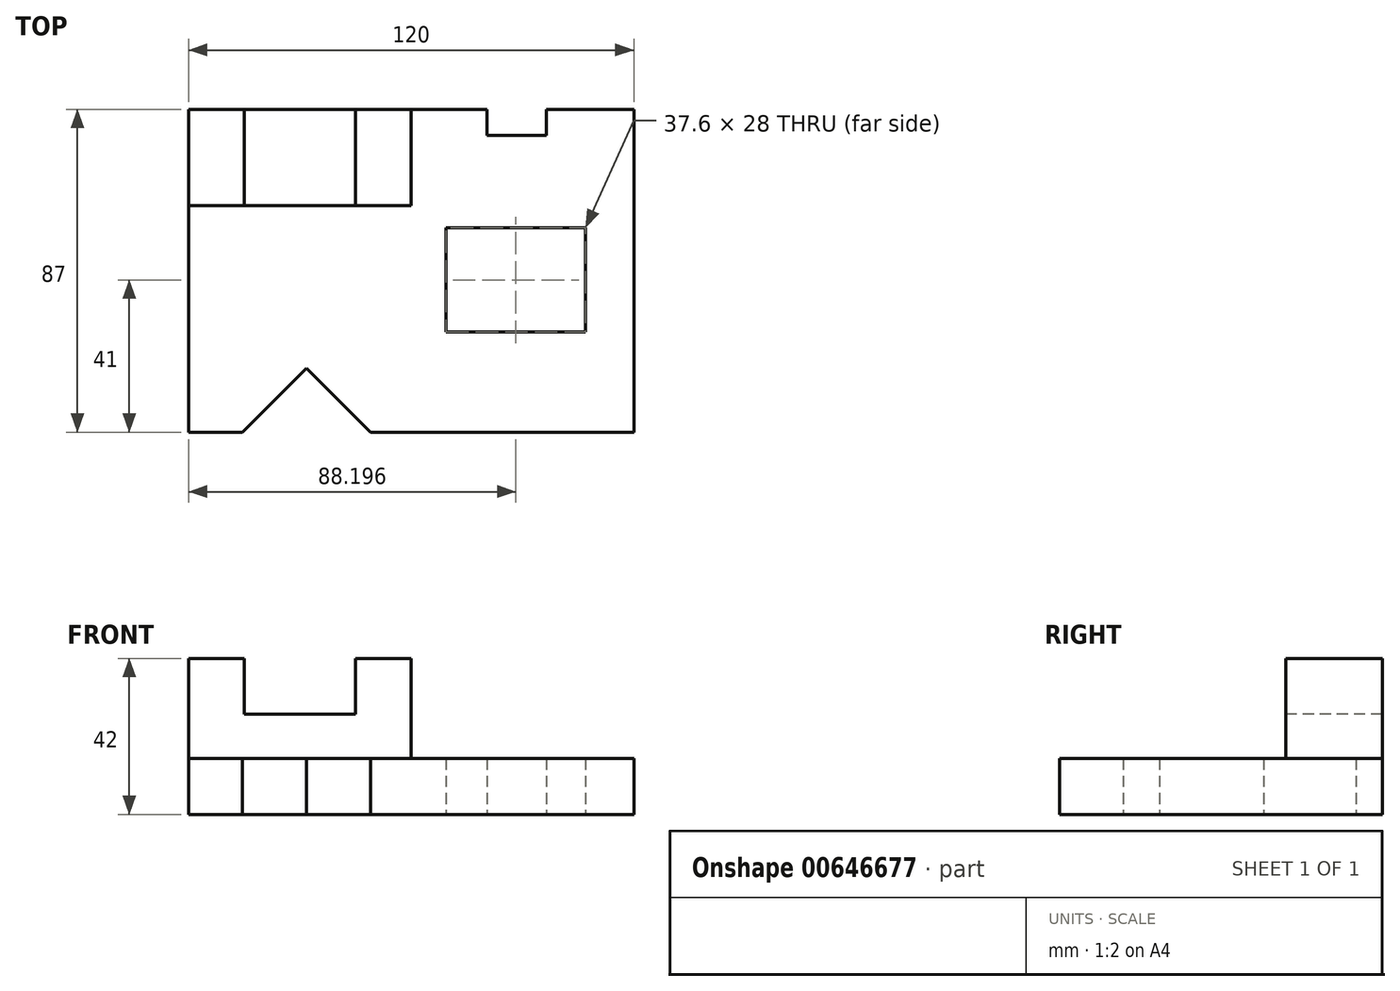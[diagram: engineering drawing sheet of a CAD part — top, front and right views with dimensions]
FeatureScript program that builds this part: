
annotation { "Feature Type Name" : "Feature", "Feature Type Description" : "" }
export const myFeature = defineFeature(function(context is Context, id is Id, definition is map)
    precondition{}
    {
        {
            var Q0;
            Q0=qCreatedBy(makeId("Top.planeOp"),FACE);
            var sketch = newSketch(context, id + "F0", { "sketchPlane" : qUnion([Q0])});
            skLineSegment(sketch, "E0", {"start": v(-373.47, 42.59) * mm, "end": v(-373.47, 103.59) * mm});
            skLineSegment(sketch, "E1", {"start": v(-373.47, 103.59) * mm, "end": v(-373.47, 129.59) * mm});
            skLineSegment(sketch, "E2", {"start": v(-373.47, 129.59) * mm, "end": v(-358.47, 129.59) * mm});
            skLineSegment(sketch, "E3", {"start": v(-358.47, 129.59) * mm, "end": v(-328.47, 129.59) * mm});
            skLineSegment(sketch, "E4", {"start": v(-328.47, 129.59) * mm, "end": v(-313.47, 129.59) * mm});
            skLineSegment(sketch, "E5", {"start": v(-313.47, 129.59) * mm, "end": v(-293.12, 129.59) * mm});
            skLineSegment(sketch, "E6", {"start": v(-293.12, 129.59) * mm, "end": v(-293.12, 122.59) * mm});
            skLineSegment(sketch, "E7", {"start": v(-293.12, 122.59) * mm, "end": v(-277.12, 122.59) * mm});
            skLineSegment(sketch, "E8", {"start": v(-277.12, 122.59) * mm, "end": v(-277.12, 129.59) * mm});
            skLineSegment(sketch, "E9", {"start": v(-277.12, 129.59) * mm, "end": v(-253.47, 129.59) * mm});
            skLineSegment(sketch, "E10", {"start": v(-253.47, 129.59) * mm, "end": v(-253.47, 42.59) * mm});
            skLineSegment(sketch, "E11", {"start": v(-253.47, 42.59) * mm, "end": v(-324.47, 42.59) * mm});
            skLineSegment(sketch, "E12", {"start": v(-358.97, 42.59) * mm, "end": v(-373.47, 42.59) * mm});
            skLineSegment(sketch, "E13", {"start": v(-373.47, 103.59) * mm, "end": v(-358.47, 103.59) * mm});
            skLineSegment(sketch, "E14", {"start": v(-358.47, 103.59) * mm, "end": v(-358.47, 129.59) * mm});
            skLineSegment(sketch, "E15", {"start": v(-358.47, 103.59) * mm, "end": v(-328.47, 103.59) * mm});
            skLineSegment(sketch, "E16", {"start": v(-328.47, 103.59) * mm, "end": v(-328.47, 129.59) * mm});
            skLineSegment(sketch, "E17", {"start": v(-328.47, 103.59) * mm, "end": v(-313.47, 103.59) * mm});
            skLineSegment(sketch, "E18", {"start": v(-313.47, 103.59) * mm, "end": v(-313.47, 129.59) * mm});
            skLineSegment(sketch, "E19", {"start": v(-266.47, 69.59) * mm, "end": v(-304.07, 69.59) * mm});
            skLineSegment(sketch, "E20", {"start": v(-304.07, 69.59) * mm, "end": v(-304.07, 97.59) * mm});
            skLineSegment(sketch, "E21", {"start": v(-304.07, 97.59) * mm, "end": v(-266.47, 97.59) * mm});
            skLineSegment(sketch, "E22", {"start": v(-266.47, 69.59) * mm, "end": v(-266.47, 97.59) * mm});
            skLineSegment(sketch, "E23", {"start": v(-341.72, 59.84) * mm, "end": v(-324.47, 42.59) * mm});
            skLineSegment(sketch, "E24", {"start": v(-341.72, 59.84) * mm, "end": v(-358.97, 42.59) * mm});
            skSolve(sketch);
        }
        {
            var Q0;
            Q0 = qSketchRegion(id + "F0", true);
            extrude(context, id + "F1", {"entities" : qUnion([Q0]), "depth" : 42 * mm, "offsetDistance" : 25 * mm});
        }
        {
            var Q0;
            Q0=makeQuery(id+"F1.opExtrude","SWEPT_FACE",FACE,{"disambiguationData":[OSD([sQuery(id+"F0.wireOp",EDGE,"E11")])]});
            var sketch = newSketch(context, id + "F2", { "sketchPlane" : qUnion([Q0])});
            skLineSegment(sketch, "E25", {"start": v(-358.47, 42) * mm, "end": v(-358.47, 27) * mm});
            skLineSegment(sketch, "E26", {"start": v(-358.47, 27) * mm, "end": v(-328.47, 27) * mm});
            skLineSegment(sketch, "E27", {"start": v(-328.47, 27) * mm, "end": v(-328.47, 42) * mm});
            skLineSegment(sketch, "E28", {"start": v(-313.47, 42) * mm, "end": v(-313.47, 15) * mm});
            skLineSegment(sketch, "E29", {"start": v(-358.47, 42) * mm, "end": v(-328.47, 42) * mm});
            skLineSegment(sketch, "E30", {"start": v(-313.47, 42) * mm, "end": v(-253.47, 42) * mm});
            skLineSegment(sketch, "E31", {"start": v(-253.47, 42) * mm, "end": v(-253.47, 15) * mm});
            skLineSegment(sketch, "E32", {"start": v(-313.47, 15) * mm, "end": v(-253.47, 15) * mm});
            skSolve(sketch);
        }
        {
            var Q0;
            Q0 = qSketchRegion(id + "F2", true);
            extrude(context, id + "F3", {"entities" : qUnion([Q0]), "operationType" : NewBodyOperationType.REMOVE, "endBound" : BoundingType.THROUGH_ALL, "oppositeDirection" : true, "depth" : 25 * mm, "offsetDistance" : 25 * mm});
        }
        {
            var Q0;
            Q0=makeQuery(id+"F1.opExtrude","SWEPT_FACE",FACE,{"disambiguationData":[OSD([sQuery(id+"F0.wireOp",EDGE,"E10")])]});
            var sketch = newSketch(context, id + "F4", { "sketchPlane" : qUnion([Q0])});
            skLineSegment(sketch, "E33", {"start": v(42.59, 15) * mm, "end": v(103.59, 15) * mm});
            skLineSegment(sketch, "E34", {"start": v(103.59, 42) * mm, "end": v(103.59, 15) * mm});
            skLineSegment(sketch, "E35", {"start": v(103.59, 42) * mm, "end": v(42.59, 42) * mm});
            skLineSegment(sketch, "E36", {"start": v(42.59, 15) * mm, "end": v(42.59, 42) * mm});
            skSolve(sketch);
        }
        {
            var Q0;
            Q0 = qSketchRegion(id + "F4", true);
            extrude(context, id + "F5", {"entities" : qUnion([Q0]), "operationType" : NewBodyOperationType.REMOVE, "endBound" : BoundingType.THROUGH_ALL, "oppositeDirection" : true, "depth" : 25 * mm, "offsetDistance" : 25 * mm});
        }
    });
